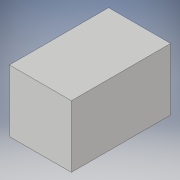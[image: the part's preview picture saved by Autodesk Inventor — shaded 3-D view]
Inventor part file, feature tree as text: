
AUTODESK INVENTOR PART (.ipt)
format: ipt  version: 2017 (Build 210142000, 142)  size: 82,432 bytes
history: native  units: in
note: dims shown in document units (in); Inventor stores cm internally (conversion verified against a paired STEP export)
features: extrude x1, sketch x1
ambient origin geometry x8: Origin, YZ Plane, XZ Plane, XY Plane, X Axis, Y Axis, Z Axis, Center Point
bodies: Solid1 (feature_tree)
feature tree (2):
  extrude  "Extrusion1"  Depth=1.25in
  sketch  "Sketch1"  dims[d0=1.25in d1=1.25in d2=2.0in d3=0.0in]
